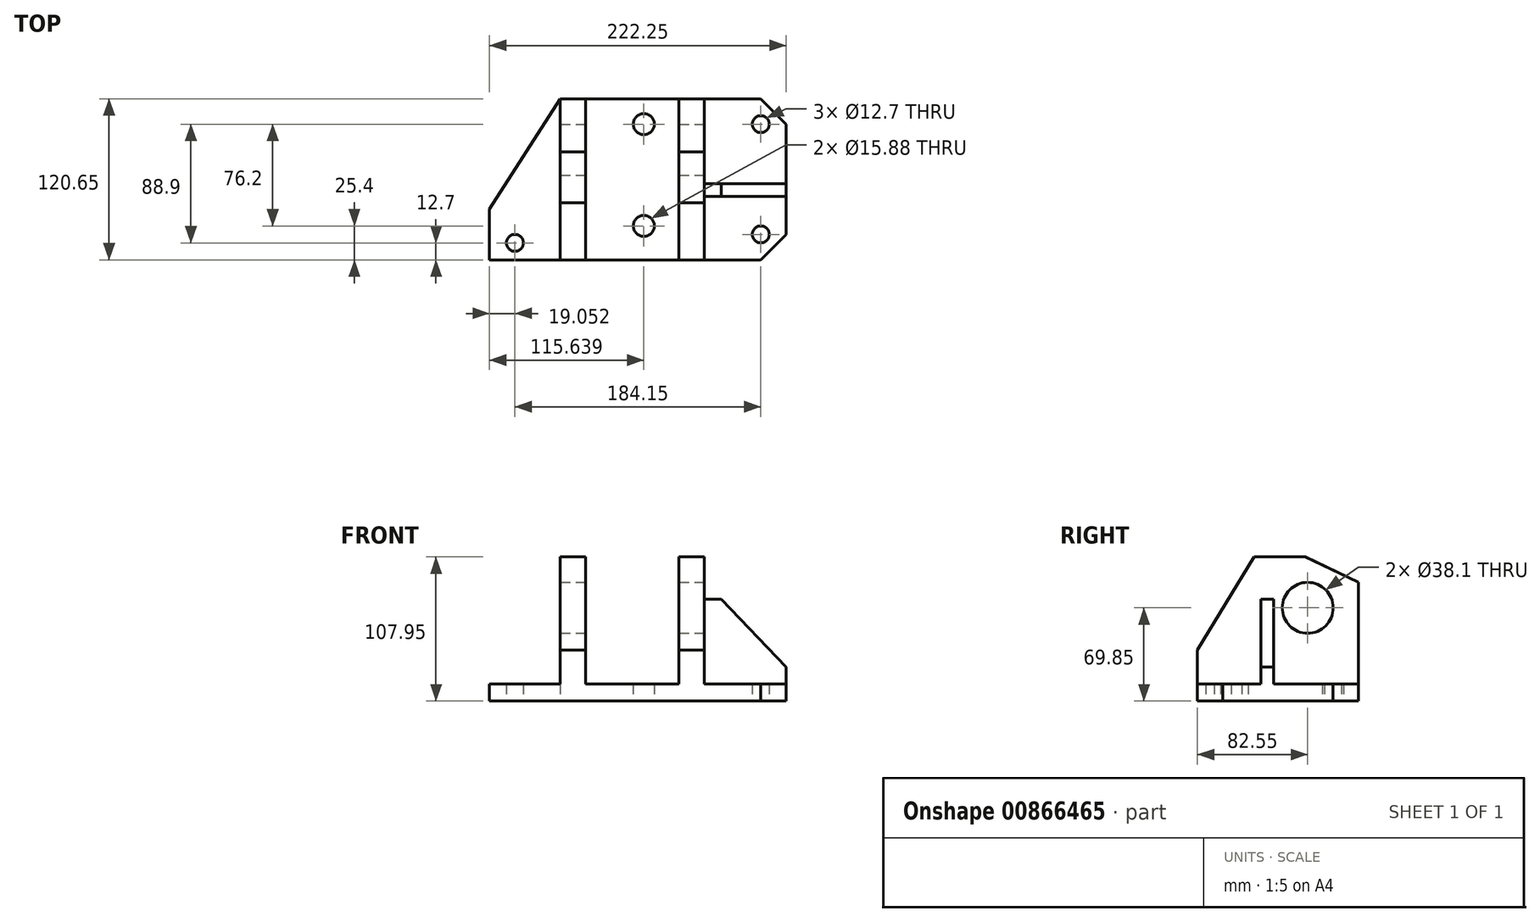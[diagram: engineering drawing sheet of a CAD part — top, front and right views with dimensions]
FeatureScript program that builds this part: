
annotation { "Feature Type Name" : "Feature", "Feature Type Description" : "" }
export const myFeature = defineFeature(function(context is Context, id is Id, definition is map)
    precondition{}
    {
        {
            var Q0;
            Q0=qCreatedBy(makeId("Top.planeOp"),FACE);
            var sketch = newSketch(context, id + "F0", { "sketchPlane" : qUnion([Q0])});
            skLineSegment(sketch, "E0", {"start": v(97.93, 82.55) * mm, "end": v(116.98, 63.5) * mm});
            skLineSegment(sketch, "E1", {"start": v(116.98, 63.5) * mm, "end": v(116.98, -19.05) * mm});
            skLineSegment(sketch, "E2", {"start": v(97.93, -38.1) * mm, "end": v(116.98, -19.05) * mm});
            skLineSegment(sketch, "E3", {"start": v(-105.27, 0) * mm, "end": v(-105.27, -38.1) * mm});
            skLineSegment(sketch, "E4.trimOffspring", {"start": v(-105.27, 0) * mm, "end": v(-52.22, 82.55) * mm});
            skLineSegment(sketch, "E5.trimOffspring", {"start": v(-105.27, -38.1) * mm, "end": v(97.93, -38.1) * mm});
            skLineSegment(sketch, "E6", {"start": v(-52.22, 82.55) * mm, "end": v(97.93, 82.55) * mm});
            skLineSegment(sketch, "E7.bottom", {"start": v(-52.22, 82.55) * mm, "end": v(-33.17, 82.55) * mm});
            skLineSegment(sketch, "E7.top", {"start": v(-52.22, -38.1) * mm, "end": v(-33.17, -38.1) * mm});
            skLineSegment(sketch, "E7.left", {"start": v(-52.22, 82.55) * mm, "end": v(-52.22, -38.1) * mm});
            skLineSegment(sketch, "E7.right", {"start": v(-33.17, 82.55) * mm, "end": v(-33.17, -38.1) * mm});
            skLineSegment(sketch, "E8", {"start": v(36.68, 82.55) * mm, "end": v(36.68, -38.1) * mm});
            skLineSegment(sketch, "E9", {"start": v(55.73, 82.55) * mm, "end": v(55.73, -38.1) * mm});
            skCircle(sketch, "E10", {"center": v(-86.22, -25.4) * mm, "radius": 6.35 * mm});
            skCircle(sketch, "E11", {"center": v(97.93, -19.05) * mm, "radius": 6.35 * mm});
            skCircle(sketch, "E12", {"center": v(97.93, 63.5) * mm, "radius": 6.35 * mm});
            skCircle(sketch, "E13", {"center": v(10.37, -12.7) * mm, "radius": 7.94 * mm});
            skCircle(sketch, "E14", {"center": v(10.37, 63.5) * mm, "radius": 7.94 * mm});
            skLineSegment(sketch, "E15", {"start": v(55.73, 9.53) * mm, "end": v(116.98, 9.53) * mm});
            skLineSegment(sketch, "E16", {"start": v(55.73, 19.05) * mm, "end": v(116.98, 19.05) * mm});
            skSolve(sketch);
        }
        {
            var Q0;
            {var subQ0=sQuery(id+"F0.wireOp",EDGE,"E15");Q0=makeQuery(id+"F0.imprint","IMPRINT",FACE,{"disambiguationData":[TD([[makeQuery(id+"F0.imprint","IMPRINT",EDGE,{"derivedFrom":subQ0}),1.0]])]});}
            var Q1;
            {var subQ0=sQuery(id+"F0.wireOp",EDGE,"E8");Q1=makeQuery(id+"F0.imprint","IMPRINT",FACE,{"disambiguationData":[TD([[makeQuery(id+"F0.imprint","IMPRINT",EDGE,{"derivedFrom":subQ0}),1.0]])]});}
            var Q2;
            {var subQ2=sQuery(id+"F0.wireOp",EDGE,"E7.left");Q2=makeQuery(id+"F0.imprint","IMPRINT",FACE,{"disambiguationData":[TD([[makeQuery(id+"F0.imprint","IMPRINT",EDGE,{"derivedFrom":subQ2}),1.0]])]});}
            var Q3;
            {var subQ1=sQuery(id+"F0.wireOp",EDGE,"E7.right");Q3=makeQuery(id+"F0.imprint","IMPRINT",FACE,{"disambiguationData":[TD([[makeQuery(id+"F0.imprint","IMPRINT",EDGE,{"derivedFrom":subQ1}),1.0]])]});}
            var Q4;
            {var subQ4=sQuery(id+"F0.wireOp",EDGE,"E2");Q4=makeQuery(id+"F0.imprint","IMPRINT",FACE,{"disambiguationData":[TD([[makeQuery(id+"F0.imprint","IMPRINT",EDGE,{"derivedFrom":subQ4}),1.0]])]});}
            var Q5;
            {var subQ1=sQuery(id+"F0.wireOp",EDGE,"E3");Q5=makeQuery(id+"F0.imprint","IMPRINT",FACE,{"disambiguationData":[TD([[makeQuery(id+"F0.imprint","IMPRINT",EDGE,{"derivedFrom":subQ1}),1.0]])]});}
            var Q6;
            {var subQ4=sQuery(id+"F0.wireOp",EDGE,"E0");Q6=makeQuery(id+"F0.imprint","IMPRINT",FACE,{"disambiguationData":[TD([[makeQuery(id+"F0.imprint","IMPRINT",EDGE,{"derivedFrom":subQ4}),-1.0]])]});}
            extrude(context, id + "F1", {"entities" : qUnion([Q0, Q1, Q2, Q3, Q4, Q5, Q6]), "depth" : 12.7 * mm, "offsetDistance" : 25.4 * mm});
        }
        {
            var Q0;
            {var subQ2=sQuery(id+"F0.wireOp",EDGE,"E7.left");Q0=makeQuery(id+"F0.imprint","IMPRINT",FACE,{"disambiguationData":[TD([[makeQuery(id+"F0.imprint","IMPRINT",EDGE,{"derivedFrom":subQ2}),1.0]])]});}
            var Q1;
            {var subQ0=sQuery(id+"F0.wireOp",EDGE,"E8");Q1=makeQuery(id+"F0.imprint","IMPRINT",FACE,{"disambiguationData":[TD([[makeQuery(id+"F0.imprint","IMPRINT",EDGE,{"derivedFrom":subQ0}),1.0]])]});}
            extrude(context, id + "F2", {"entities" : qUnion([Q0, Q1]), "operationType" : NewBodyOperationType.ADD, "depth" : 107.95 * mm, "offsetDistance" : 25.4 * mm});
        }
        {
            var Q0;
            {var subQ0=sQuery(id+"F0.wireOp",EDGE,"E15");Q0=makeQuery(id+"F0.imprint","IMPRINT",FACE,{"disambiguationData":[TD([[makeQuery(id+"F0.imprint","IMPRINT",EDGE,{"derivedFrom":subQ0}),1.0]])]});}
            extrude(context, id + "F3", {"entities" : qUnion([Q0]), "operationType" : NewBodyOperationType.ADD, "depth" : 76.2 * mm, "offsetDistance" : 25.4 * mm});
        }
        {
            var Q0;
            Q0=makeQuery(id+"F3.opExtrude","SWEPT_FACE",FACE,{"disambiguationData":[OSD([sQuery(id+"F0.wireOp",EDGE,"E15")])]});
            var sketch = newSketch(context, id + "F4", { "sketchPlane" : qUnion([Q0])});
            skLineSegment(sketch, "E17", {"start": v(116.98, 25.4) * mm, "end": v(68.43, 76.2) * mm});
            skSolve(sketch);
        }
        {
            var Q0;
            Q0 = qSketchRegion(id + "F4", true);
            var Q1;
            {var subQ0=sQuery(id+"F4.wireOp",EDGE,"E17");Q1=makeQuery(id+"F4.imprint","IMPRINT",FACE,{"disambiguationData":[TD([[makeQuery(id+"F4.imprint","IMPRINT",EDGE,{"derivedFrom":subQ0}),-1.0]])]});}
            extrude(context, id + "F5", {"entities" : qUnion([Q0, Q1]), "operationType" : NewBodyOperationType.REMOVE, "oppositeDirection" : true, "depth" : 25.4 * mm, "offsetDistance" : 25.4 * mm});
        }
        {
            var Q0;
            Q0=makeQuery(id+"F2.opExtrude","SWEPT_FACE",FACE,{"disambiguationData":[OSD([sQuery(id+"F0.wireOp",EDGE,"E7.right")])]});
            var sketch = newSketch(context, id + "F6", { "sketchPlane" : qUnion([Q0])});
            skLineSegment(sketch, "E18", {"start": v(42.87, 107.95) * mm, "end": v(82.55, 88.9) * mm});
            skLineSegment(sketch, "E19", {"start": v(4.77, 107.95) * mm, "end": v(-38.1, 38.1) * mm});
            skCircle(sketch, "E20", {"center": v(44.45, 69.85) * mm, "radius": 19.05 * mm});
            skSolve(sketch);
        }
        {
            var Q0;
            Q0 = qSketchRegion(id + "F6", true);
            var Q1;
            {var subQ0=sQuery(id+"F6.wireOp",EDGE,"E19");Q1=makeQuery(id+"F6.imprint","IMPRINT",FACE,{"disambiguationData":[TD([[makeQuery(id+"F6.imprint","IMPRINT",EDGE,{"derivedFrom":subQ0}),-1.0]])]});}
            var Q2;
            {var subQ0=sQuery(id+"F6.wireOp",EDGE,"E18");Q2=makeQuery(id+"F6.imprint","IMPRINT",FACE,{"disambiguationData":[TD([[makeQuery(id+"F6.imprint","IMPRINT",EDGE,{"derivedFrom":subQ0}),1.0]])]});}
            extrude(context, id + "F7", {"entities" : qUnion([Q0, Q1, Q2]), "operationType" : NewBodyOperationType.REMOVE, "oppositeDirection" : true, "depth" : 76.7 * mm, "offsetDistance" : 25.4 * mm});
        }
        {
            var Q0;
            Q0=makeQuery(id+"F2.opExtrude","SWEPT_FACE",FACE,{"disambiguationData":[OSD([sQuery(id+"F0.wireOp",EDGE,"E9")])]});
            var sketch = newSketch(context, id + "F8", { "sketchPlane" : qUnion([Q0])});
            skLineSegment(sketch, "E21", {"start": v(-38.1, 38.1) * mm, "end": v(4.48, 107.95) * mm});
            skLineSegment(sketch, "E22", {"start": v(42.58, 107.95) * mm, "end": v(82.55, 88.9) * mm});
            skCircle(sketch, "E23", {"center": v(44.45, 69.85) * mm, "radius": 19.05 * mm});
            skSolve(sketch);
        }
        {
            var Q0;
            {var subQ0=sQuery(id+"F8.wireOp",EDGE,"E21");Q0=makeQuery(id+"F8.imprint","IMPRINT",FACE,{"disambiguationData":[TD([[makeQuery(id+"F8.imprint","IMPRINT",EDGE,{"derivedFrom":subQ0}),1.0]])]});}
            var Q1;
            {var subQ0=sQuery(id+"F8.wireOp",EDGE,"E22");Q1=makeQuery(id+"F8.imprint","IMPRINT",FACE,{"disambiguationData":[TD([[makeQuery(id+"F8.imprint","IMPRINT",EDGE,{"derivedFrom":subQ0}),1.0]])]});}
            var Q2;
            Q2=makeQuery(id+"F8.imprint","IMPRINT",FACE,{"disambiguationData":[TD([[makeQuery(id+"F8.imprint","IMPRINT",EDGE,{"derivedFrom":sQuery(id+"F8.wireOp",EDGE,"E23")}),1.0]])]});
            extrude(context, id + "F9", {"entities" : qUnion([Q0, Q1, Q2]), "operationType" : NewBodyOperationType.REMOVE, "oppositeDirection" : true, "depth" : 25.4 * mm, "offsetDistance" : 25.4 * mm});
        }
    });
